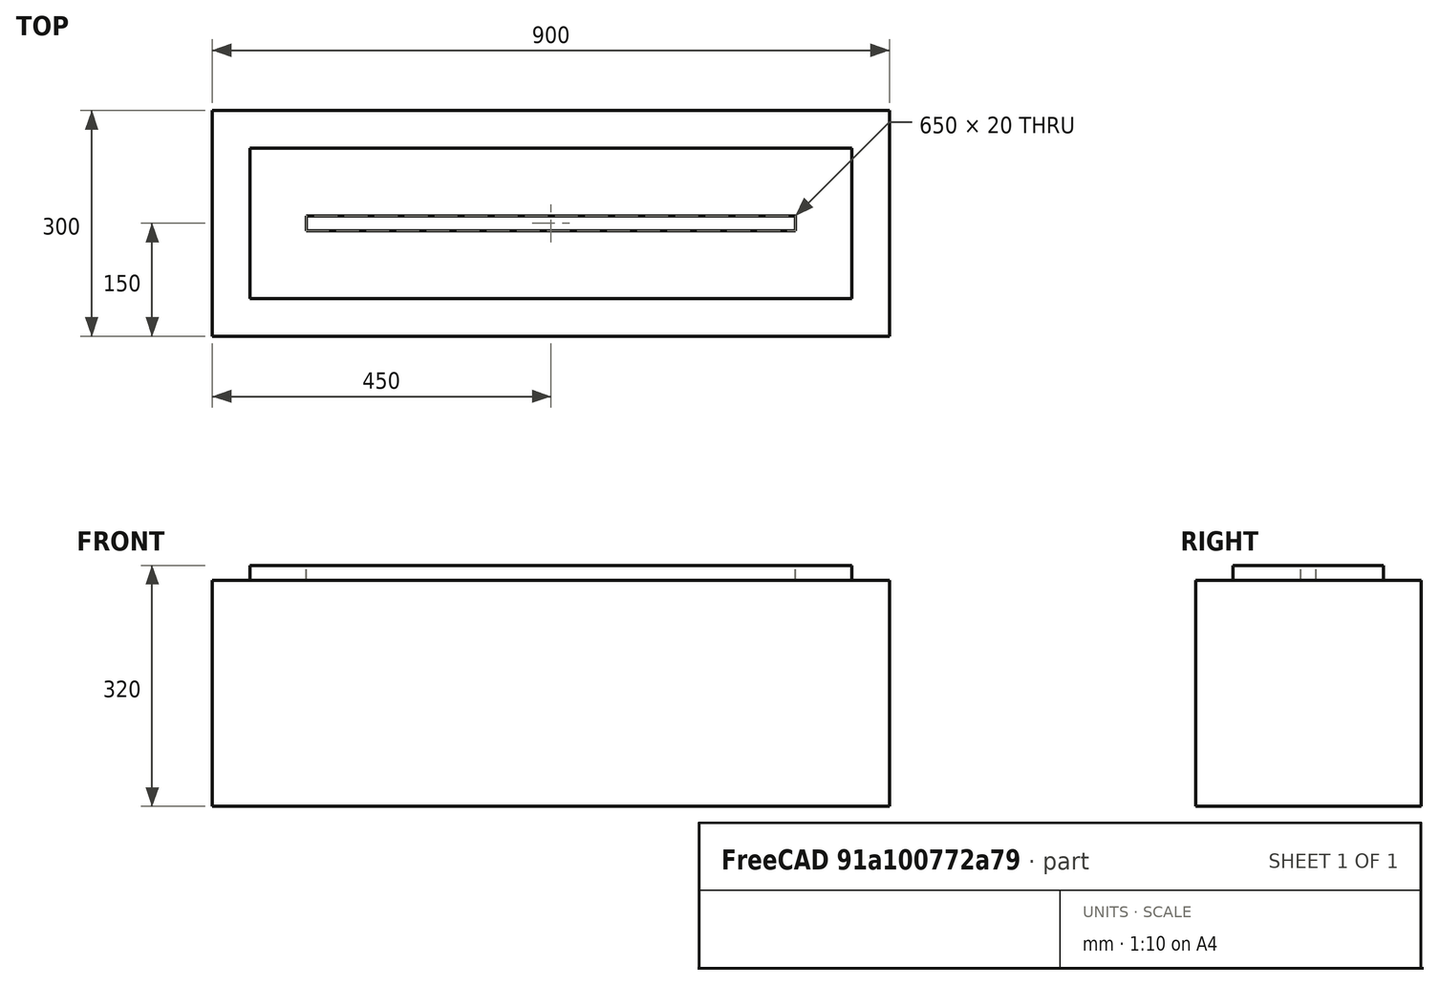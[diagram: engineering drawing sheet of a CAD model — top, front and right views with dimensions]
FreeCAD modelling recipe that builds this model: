
FCSTD DOCUMENT  (FreeCAD 0.21R33668 +26 (Git))
Label: Lareira a gás
License: All rights reserved
objects: Part::Part2DObjectPython×3, Part::Extrusion×3, Part::Cut×1, Part::Compound×1
note: 8 computed .brp shape members not serialized (recipe doc carries the construction recipe); baked Part::Feature solids carry a one-line shape summary decoded from their .brp

FEATURE [Part::Part2DObjectPython] Rectangle025  # Draft 2D object (typed FeaturePython)
  Area = 270000
  ChamferSize = 0
  Columns = 1
  FilletRadius = 0
  Height = 900
  Length = 300
  MakeFace = true
  Rows = 1
FEATURE [Part::Extrusion] Extrude061  label="Extrude090"
  Base = -> Rectangle025
  Dir = (0,0,1)
  DirMode = 2
  FaceMakerClass = Part::FaceMakerBullseye
  LengthFwd = 300
  LengthRev = 0
  Solid = false
  Symmetric = false
FEATURE [Part::Part2DObjectPython] Rectangle026  # Draft 2D object (typed FeaturePython)
  Area = 160000
  ChamferSize = 0
  Columns = 1
  FilletRadius = 0
  Height = 800
  Length = 200
  MakeFace = true
  Placement = pos=(207.601,206.496,400) rot=(0,0,1;0rad)
  Rows = 1
FEATURE [Part::Extrusion] Extrude062
  Base = -> Rectangle026
  Dir = (0,0,1)
  DirMode = 2
  FaceMakerClass = Part::FaceMakerBullseye
  LengthFwd = 20
  LengthRev = 0
  Placement = pos=(-157.601,-156.496,-100) rot=(0,0,1;0rad)
  Solid = false
  Symmetric = false
FEATURE [Part::Part2DObjectPython] Rectangle027  # Draft 2D object (typed FeaturePython)
  Area = 13000
  ChamferSize = 0
  Columns = 1
  FilletRadius = 0
  Height = 650
  Length = 20
  MakeFace = true
  Placement = pos=(289.621,275.316,420) rot=(0,0,1;0rad)
  Rows = 1
FEATURE [Part::Extrusion] Extrude063
  Base = -> Rectangle027
  Dir = (0,0,1)
  DirMode = 2
  FaceMakerClass = Part::FaceMakerBullseye
  LengthFwd = 0
  LengthRev = 20
  Placement = pos=(-149.621,-150.316,-100) rot=(0,0,1;0rad)
  Solid = false
  Symmetric = false
FEATURE [Part::Cut] Cut015
  Base = -> Extrude062
  Tool = -> Extrude063
FEATURE [Part::Compound] Compound017  label="Lareira"
  Links = -> [Extrude061,Cut015]
  Placement = pos=(0,0,0) rot=(0,0,1;1.5708rad)
